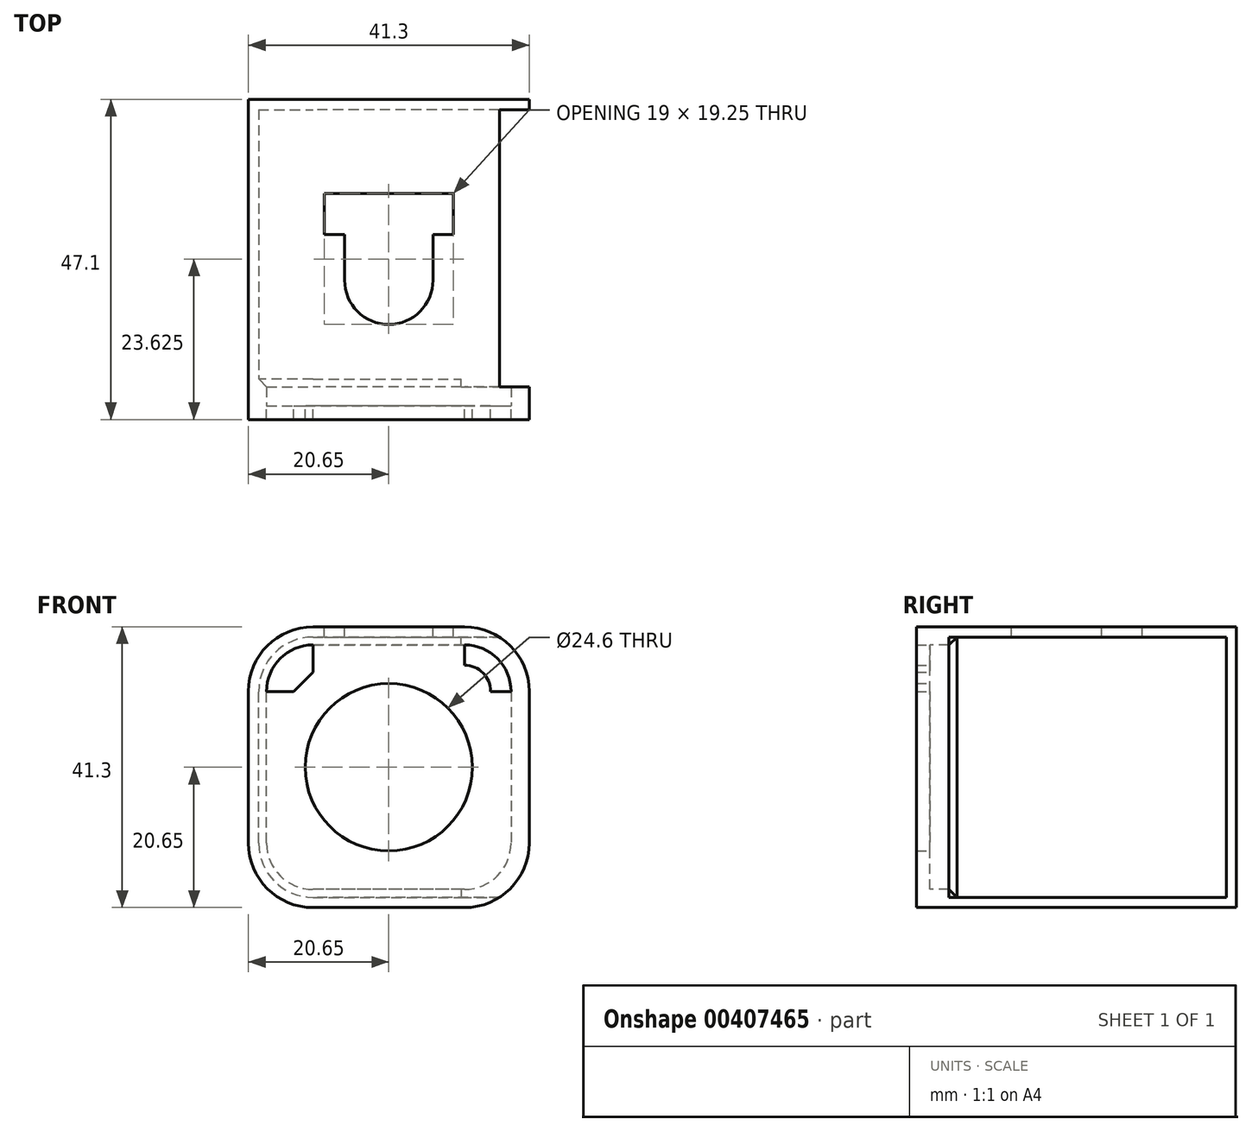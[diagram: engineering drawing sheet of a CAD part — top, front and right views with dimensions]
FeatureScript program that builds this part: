
annotation { "Feature Type Name" : "Feature", "Feature Type Description" : "" }
export const myFeature = defineFeature(function(context is Context, id is Id, definition is map)
    precondition{}
    {
        {
            var Q0;
            Q0=qCreatedBy(makeId("Front.planeOp"),FACE);
            var sketch = newSketch(context, id + "F0", { "sketchPlane" : qUnion([Q0])});
            skLineSegment(sketch, "E0.bottom", {"start": v(11.15, 19.15) * mm, "end": v(-11.15, 19.15) * mm});
            skLineSegment(sketch, "E0.top", {"start": v(11.15, -19.15) * mm, "end": v(-11.15, -19.15) * mm});
            skLineSegment(sketch, "E0.left", {"start": v(19.15, 11.15) * mm, "end": v(19.15, -11.15) * mm});
            skLineSegment(sketch, "E0.right", {"start": v(-19.15, 11.15) * mm, "end": v(-19.15, -11.15) * mm});
            skPoint(sketch, "E0.middle", {"position": v(0, 0) * mm});
            skPoint(sketch, "E1.visualSharp", {"position": v(-19.15, 19.15) * mm});
            skArc(sketch, "E1.filletArc", {"start": v(-11.15, 19.15) * mm, "mid": v(-16.8, 16.8) * mm, "end": v(-19.15, 11.15) * mm});
            skPoint(sketch, "E2.visualSharp", {"position": v(19.15, 19.15) * mm});
            skArc(sketch, "E2.filletArc", {"start": v(19.15, 11.15) * mm, "mid": v(16.8, 16.8) * mm, "end": v(11.15, 19.15) * mm});
            skPoint(sketch, "E3.visualSharp", {"position": v(19.15, -19.15) * mm});
            skArc(sketch, "E3.filletArc", {"start": v(11.15, -19.15) * mm, "mid": v(16.8, -16.8) * mm, "end": v(19.15, -11.15) * mm});
            skPoint(sketch, "E4.visualSharp", {"position": v(-19.15, -19.15) * mm});
            skArc(sketch, "E4.filletArc", {"start": v(-19.15, -11.15) * mm, "mid": v(-16.8, -16.8) * mm, "end": v(-11.15, -19.15) * mm});
            skLineSegment(sketch, "E5.0", {"start": v(11.15, 20.65) * mm, "end": v(-11.15, 20.65) * mm});
            skArc(sketch, "E5.1", {"start": v(20.65, 11.15) * mm, "mid": v(17.87, 17.87) * mm, "end": v(11.15, 20.65) * mm});
            skArc(sketch, "E5.2", {"start": v(-11.15, 20.65) * mm, "mid": v(-17.87, 17.87) * mm, "end": v(-20.65, 11.15) * mm});
            skLineSegment(sketch, "E5.3", {"start": v(20.65, 11.15) * mm, "end": v(20.65, -11.15) * mm});
            skLineSegment(sketch, "E5.4", {"start": v(-20.65, 11.15) * mm, "end": v(-20.65, -11.15) * mm});
            skArc(sketch, "E5.5", {"start": v(-20.65, -11.15) * mm, "mid": v(-17.87, -17.87) * mm, "end": v(-11.15, -20.65) * mm});
            skLineSegment(sketch, "E5.6", {"start": v(11.15, -20.65) * mm, "end": v(-11.15, -20.65) * mm});
            skArc(sketch, "E5.7", {"start": v(11.15, -20.65) * mm, "mid": v(17.87, -17.87) * mm, "end": v(20.65, -11.15) * mm});
            skLineSegment(sketch, "E6.0", {"start": v(11.15, 17.98) * mm, "end": v(-11.15, 17.98) * mm});
            skArc(sketch, "E6.1", {"start": v(17.98, 11.15) * mm, "mid": v(15.98, 15.98) * mm, "end": v(11.15, 17.98) * mm});
            skArc(sketch, "E6.2", {"start": v(-11.15, 17.98) * mm, "mid": v(-15.98, 15.98) * mm, "end": v(-17.98, 11.15) * mm});
            skLineSegment(sketch, "E6.3", {"start": v(17.98, 11.15) * mm, "end": v(17.98, -11.15) * mm});
            skLineSegment(sketch, "E6.4", {"start": v(-17.98, 11.15) * mm, "end": v(-17.98, -11.15) * mm});
            skArc(sketch, "E6.5", {"start": v(-17.98, -11.15) * mm, "mid": v(-15.98, -15.98) * mm, "end": v(-11.15, -17.98) * mm});
            skLineSegment(sketch, "E6.6", {"start": v(11.15, -17.98) * mm, "end": v(-11.15, -17.98) * mm});
            skArc(sketch, "E6.7", {"start": v(11.15, -17.98) * mm, "mid": v(15.98, -15.98) * mm, "end": v(17.98, -11.15) * mm});
            skSolve(sketch);
        }
        {
            var Q0;
            Q0=makeQuery(id+"F0.imprint","IMPRINT",FACE,{"disambiguationData":[TD([[makeQuery(id+"F0.imprint","IMPRINT",EDGE,{"derivedFrom":sQuery(id+"F0.wireOp",EDGE,"E0.bottom")}),-1.0]])]});
            var Q1;
            Q1=makeQuery(id+"F0.imprint","IMPRINT",FACE,{"disambiguationData":[TD([[makeQuery(id+"F0.imprint","IMPRINT",EDGE,{"derivedFrom":sQuery(id+"F0.wireOp",EDGE,"E5.5")}),-1.0]])]});
            extrude(context, id + "F1", {"entities" : qUnion([Q0, Q1]), "oppositeDirection" : true, "depth" : 43.6 * mm});
        }
        {
            var Q0;
            Q0=makeQuery(id+"F0.imprint","IMPRINT",FACE,{"disambiguationData":[TD([[makeQuery(id+"F0.imprint","IMPRINT",EDGE,{"derivedFrom":sQuery(id+"F0.wireOp",EDGE,"E0.bottom")}),1.0]])]});
            var Q1;
            Q1=makeQuery(id+"F0.imprint","IMPRINT",FACE,{"disambiguationData":[TD([[makeQuery(id+"F0.imprint","IMPRINT",EDGE,{"derivedFrom":sQuery(id+"F0.wireOp",EDGE,"E0.bottom")}),-1.0]])]});
            extrude(context, id + "F2", {"entities" : qUnion([Q0, Q1]), "operationType" : NewBodyOperationType.ADD, "oppositeDirection" : true, "depth" : 4 * mm});
        }
        {
            var Q0;
            Q0=makeQuery(id+"F2.opExtrude","CAP_EDGE",EDGE,{"disambiguationData":[OSD([sQuery(id+"F0.wireOp",EDGE,"E6.2")])],"isStart":false});
            var Q1;
            Q1=makeQuery(id+"F2.opExtrude","CAP_EDGE",EDGE,{"disambiguationData":[OSD([sQuery(id+"F0.wireOp",EDGE,"E6.4")])],"isStart":false});
            var Q2;
            Q2=makeQuery(id+"F2.opExtrude","CAP_EDGE",EDGE,{"disambiguationData":[OSD([sQuery(id+"F0.wireOp",EDGE,"E6.5")])],"isStart":false});
            var Q3;
            Q3=makeQuery(id+"F2.opExtrude","CAP_EDGE",EDGE,{"disambiguationData":[OSD([sQuery(id+"F0.wireOp",EDGE,"E6.6")])],"isStart":false});
            var Q4;
            Q4=makeQuery(id+"F2.opExtrude","CAP_EDGE",EDGE,{"disambiguationData":[OSD([sQuery(id+"F0.wireOp",EDGE,"E6.7")])],"isStart":false});
            var Q5;
            Q5=makeQuery(id+"F2.opExtrude","CAP_EDGE",EDGE,{"disambiguationData":[OSD([sQuery(id+"F0.wireOp",EDGE,"E6.3")])],"isStart":false});
            var Q6;
            Q6=makeQuery(id+"F2.opExtrude","CAP_EDGE",EDGE,{"disambiguationData":[OSD([sQuery(id+"F0.wireOp",EDGE,"E6.1")])],"isStart":false});
            var Q7;
            Q7=makeQuery(id+"F2.opExtrude","CAP_EDGE",EDGE,{"disambiguationData":[OSD([sQuery(id+"F0.wireOp",EDGE,"E6.0")])],"isStart":false});
            chamfer(context, id + "F3", {"entities" : qUnion([Q0, Q1, Q2, Q3, Q4, Q5, Q6, Q7]), "width" : 1.2 * mm, "tangentPropagation" : true});
        }
        {
            var Q0;
            Q0=makeQuery(id+"F1.opExtrude","SWEPT_FACE",FACE,{"disambiguationData":[OSD([sQuery(id+"F0.wireOp",EDGE,"E5.0")])]});
            var sketch = newSketch(context, id + "F4", { "sketchPlane" : qUnion([Q0])});
            skCircle(sketch, "E7", {"center": v(0, 18.5) * mm, "radius": 6.5 * mm});
            skLineSegment(sketch, "E8.bottom", {"start": v(-9.5, 25.25) * mm, "end": v(9.5, 25.25) * mm});
            skLineSegment(sketch, "E8.top", {"start": v(-9.5, 31.25) * mm, "end": v(9.5, 31.25) * mm});
            skLineSegment(sketch, "E8.left", {"start": v(-9.5, 25.25) * mm, "end": v(-9.5, 31.25) * mm});
            skLineSegment(sketch, "E8.right", {"start": v(9.5, 25.25) * mm, "end": v(9.5, 31.25) * mm});
            skPoint(sketch, "E8.middle", {"position": v(0, 28.25) * mm});
            skLineSegment(sketch, "E9", {"start": v(-6.5, 18.5) * mm, "end": v(-6.5, 25.25) * mm});
            skLineSegment(sketch, "E10", {"start": v(6.5, 18.5) * mm, "end": v(6.5, 25.25) * mm});
            skSolve(sketch);
        }
        {
            var Q0;
            Q0=makeQuery(id+"F4.imprint","IMPRINT",FACE,{"disambiguationData":[TD([[makeQuery(id+"F4.imprint","IMPRINT",EDGE,{"derivedFrom":sQuery(id+"F4.wireOp",EDGE,"E8.bottom")}),1.0]])]});
            var Q1;
            Q1=makeQuery(id+"F4.imprint","IMPRINT",FACE,{"disambiguationData":[TD([[makeQuery(id+"F4.imprint","IMPRINT",EDGE,{"derivedFrom":sQuery(id+"F4.wireOp",EDGE,"E7")}),1.0]])]});
            var Q2;
            {var subQ0=sQuery(id+"F4.wireOp",EDGE,"E9");Q2=makeQuery(id+"F4.imprint","IMPRINT",FACE,{"disambiguationData":[TD([[makeQuery(id+"F4.imprint","IMPRINT",EDGE,{"derivedFrom":subQ0}),-1.0]])]});}
            extrude(context, id + "F5", {"entities" : qUnion([Q0, Q1, Q2]), "operationType" : NewBodyOperationType.REMOVE, "oppositeDirection" : true, "depth" : 5 * mm});
        }
        {
            var Q0;
            {var subQ0=sQuery(id+"F0.wireOp",EDGE,"E5.4");var subQ1=sQuery(id+"F0.wireOp",EDGE,"E5.3");var subQ2=sQuery(id+"F0.wireOp",EDGE,"E5.2");var subQ3=sQuery(id+"F0.wireOp",EDGE,"E5.1");var subQ4=sQuery(id+"F0.wireOp",EDGE,"E5.0");Q0=makeQuery(id+"F2.boolean.opBoolean","MERGE",FACE,{"derivedFrom":[makeQuery(id+"F1.opExtrude","CAP_FACE",FACE,{"disambiguationData":[OSD([sQuery(id+"F0.wireOp",EDGE,"E0.bottom"),sQuery(id+"F0.wireOp",EDGE,"E0.top"),sQuery(id+"F0.wireOp",EDGE,"E0.left"),sQuery(id+"F0.wireOp",EDGE,"E0.right"),sQuery(id+"F0.wireOp",EDGE,"E1.filletArc"),sQuery(id+"F0.wireOp",EDGE,"E2.filletArc"),sQuery(id+"F0.wireOp",EDGE,"E3.filletArc"),sQuery(id+"F0.wireOp",EDGE,"E4.filletArc"),subQ4,subQ3,subQ2,subQ1,subQ0,sQuery(id+"F0.wireOp",EDGE,"1ce2179c-068b-4943-9692-729ea4e3db66"),sQuery(id+"F0.wireOp",EDGE,"7OH42xqO-JseY-yhtM-Qi2A-LRlWQrP5thO4"),sQuery(id+"F0.wireOp",EDGE,"44586aa2-9acb-4dc7-b725-257d72291ac40.MirrorCS"),sQuery(id+"F0.wireOp",EDGE,"e682bec5-039f-430b-ad56-1ab046a109670.MirrorCS")])],"isStart":true}),makeQuery(id+"F2.opExtrude","CAP_FACE",FACE,{"disambiguationData":[OSD([subQ4,subQ3,subQ2,subQ1,subQ0,sQuery(id+"F0.wireOp",EDGE,"E5.5"),sQuery(id+"F0.wireOp",EDGE,"E5.6"),sQuery(id+"F0.wireOp",EDGE,"E5.7"),sQuery(id+"F0.wireOp",EDGE,"E6.0"),sQuery(id+"F0.wireOp",EDGE,"E6.1"),sQuery(id+"F0.wireOp",EDGE,"E6.2"),sQuery(id+"F0.wireOp",EDGE,"E6.3"),sQuery(id+"F0.wireOp",EDGE,"E6.4"),sQuery(id+"F0.wireOp",EDGE,"E6.5"),sQuery(id+"F0.wireOp",EDGE,"E6.6"),sQuery(id+"F0.wireOp",EDGE,"E6.7")])],"isStart":true})]});}
            var sketch = newSketch(context, id + "F6", { "sketchPlane" : qUnion([Q0])});
            skCircle(sketch, "E11", {"center": v(0, 0) * mm, "radius": 12.3 * mm});
            skArc(sketch, "E12.0", {"start": v(14.98, 11.15) * mm, "mid": v(13.86, 13.86) * mm, "end": v(11.15, 14.98) * mm});
            skLineSegment(sketch, "E13", {"start": v(11.15, 14.98) * mm, "end": v(11.15, 17.98) * mm});
            skLineSegment(sketch, "E14", {"start": v(14.98, 11.15) * mm, "end": v(17.98, 11.15) * mm});
            skLineSegment(sketch, "E15", {"start": v(0, 17.98) * mm, "end": v(0, -17.98) * mm, "construction": true});
            skLineSegment(sketch, "E16", {"start": v(-17.98, 11.15) * mm, "end": v(-13.99, 11.15) * mm});
            skLineSegment(sketch, "E17", {"start": v(-11.15, 17.98) * mm, "end": v(-11.15, 13.99) * mm});
            skLineSegment(sketch, "E18", {"start": v(-13.99, 11.15) * mm, "end": v(-11.15, 13.99) * mm});
            skSolve(sketch);
        }
        {
            var Q0;
            Q0=makeQuery(id+"F6.imprint","IMPRINT",FACE,{"disambiguationData":[TD([[makeQuery(id+"F6.imprint","IMPRINT",EDGE,{"derivedFrom":sQuery(id+"F6.wireOp",EDGE,"E11")}),-1.0]])]});
            var Q1;
            {var subQ5=sQuery(id+"F0.wireOp",EDGE,"E5.0");Q1=makeQuery(id+"F6.imprint","IMPRINT",FACE,{"disambiguationData":[TD([[makeQuery(id+"F6.imprint","IMPRINT",EDGE,{"derivedFrom":makeQuery(id+"F1.opExtrude","CAP_EDGE",EDGE,{"disambiguationData":[OSD([subQ5])],"isStart":true})}),1.0]])]});}
            extrude(context, id + "F7", {"entities" : qUnion([Q0, Q1]), "operationType" : NewBodyOperationType.ADD, "depth" : 2 * mm});
        }
        {
            var Q0;
            Q0=makeQuery(id+"F1.opExtrude","CAP_FACE",FACE,{"disambiguationData":[OSD([sQuery(id+"F0.wireOp",EDGE,"E0.bottom"),sQuery(id+"F0.wireOp",EDGE,"E0.top"),sQuery(id+"F0.wireOp",EDGE,"E0.left"),sQuery(id+"F0.wireOp",EDGE,"E0.right"),sQuery(id+"F0.wireOp",EDGE,"E1.filletArc"),sQuery(id+"F0.wireOp",EDGE,"E2.filletArc"),sQuery(id+"F0.wireOp",EDGE,"E3.filletArc"),sQuery(id+"F0.wireOp",EDGE,"E4.filletArc"),sQuery(id+"F0.wireOp",EDGE,"E5.0"),sQuery(id+"F0.wireOp",EDGE,"E5.1"),sQuery(id+"F0.wireOp",EDGE,"E5.2"),sQuery(id+"F0.wireOp",EDGE,"E5.3"),sQuery(id+"F0.wireOp",EDGE,"E5.4"),sQuery(id+"F0.wireOp",EDGE,"E5.5"),sQuery(id+"F0.wireOp",EDGE,"E5.6"),sQuery(id+"F0.wireOp",EDGE,"E5.7")])],"isStart":false});
            var sketch = newSketch(context, id + "F8", { "sketchPlane" : qUnion([Q0])});
            skSolve(sketch);
        }
        {
            var Q0;
            Q0=makeQuery(id+"F8.imprint","IMPRINT",FACE,{"disambiguationData":[TD([[makeQuery(id+"F8.imprint","IMPRINT",EDGE,{"derivedFrom":makeQuery(id+"F1.opExtrude","CAP_EDGE",EDGE,{"disambiguationData":[OSD([sQuery(id+"F0.wireOp",EDGE,"E0.bottom")])],"isStart":false})}),-1.0]])]});
            var Q1;
            Q1=makeQuery(id+"F8.imprint","IMPRINT",FACE,{"disambiguationData":[TD([[makeQuery(id+"F8.imprint","IMPRINT",EDGE,{"derivedFrom":makeQuery(id+"F1.opExtrude","CAP_EDGE",EDGE,{"disambiguationData":[OSD([sQuery(id+"F0.wireOp",EDGE,"E0.bottom")])],"isStart":false})}),1.0]])]});
            extrude(context, id + "F9", {"entities" : qUnion([Q0, Q1]), "operationType" : NewBodyOperationType.ADD, "depth" : 1.5 * mm});
        }
        {
            var Q0;
            Q0=makeQuery(id+"F1.opExtrude","SWEPT_FACE",FACE,{"disambiguationData":[OSD([sQuery(id+"F0.wireOp",EDGE,"E5.3")])]});
            var sketch = newSketch(context, id + "F10", { "sketchPlane" : qUnion([Q0])});
            skLineSegment(sketch, "E19.bottom", {"start": v(2.8, 19.15) * mm, "end": v(43.6, 19.15) * mm});
            skLineSegment(sketch, "E19.top", {"start": v(2.8, -19.15) * mm, "end": v(43.6, -19.15) * mm});
            skLineSegment(sketch, "E19.left", {"start": v(2.8, 19.15) * mm, "end": v(2.8, -19.15) * mm});
            skLineSegment(sketch, "E19.right", {"start": v(43.6, 19.15) * mm, "end": v(43.6, -19.15) * mm});
            skSolve(sketch);
        }
        {
            var Q0;
            {var subQ0=sQuery(id+"F10.wireOp",EDGE,"E19.bottom");Q0=makeQuery(id+"F10.imprint","IMPRINT",FACE,{"disambiguationData":[TD([[makeQuery(id+"F10.imprint","IMPRINT",EDGE,{"derivedFrom":subQ0}),-1.0]])]});}
            var Q1;
            {var subQ0=sQuery(id+"F10.wireOp",EDGE,"E19.left");var subQ1=sQuery(id+"F0.wireOp",EDGE,"E5.3");var subQ2=sQuery(id+"F0.wireOp",EDGE,"E5.1");var subQ3=makeQuery(id+"F9.boolean.opBoolean","MERGE",EDGE,{"derivedFrom":[makeQuery(id+"F7.boolean.opBoolean","MERGE",EDGE,{"derivedFrom":[makeQuery(id+"F1.opExtrude","SWEPT_EDGE",EDGE,{"disambiguationData":[OSD([subQ2,subQ1])]}),makeQuery(id+"F7.opExtrude","SWEPT_EDGE",EDGE,{"disambiguationData":[OSD([subQ2,subQ1])]})]}),makeQuery(id+"F9.opExtrude","SWEPT_EDGE",EDGE,{"disambiguationData":[OSD([subQ2,subQ1])]})]});var subQ4=makeQuery(id+"F10.imprint","INTERSECT",VERTEX,{"derivedFrom":[subQ3,subQ0]});Q1=makeQuery(id+"F10.imprint","IMPRINT",FACE,{"disambiguationData":[TD([[makeQuery(id+"F10.imprint","IMPRINT",EDGE,{"disambiguationData":[TD([[subQ4,-1.0]])],"derivedFrom":subQ0}),1.0]])]});}
            var Q2;
            {var subQ0=sQuery(id+"F10.wireOp",EDGE,"E19.top");Q2=makeQuery(id+"F10.imprint","IMPRINT",FACE,{"disambiguationData":[TD([[makeQuery(id+"F10.imprint","IMPRINT",EDGE,{"derivedFrom":subQ0}),1.0]])]});}
            extrude(context, id + "F11", {"entities" : qUnion([Q0, Q1, Q2]), "operationType" : NewBodyOperationType.REMOVE, "oppositeDirection" : true, "depth" : 10 * mm});
        }
    });
